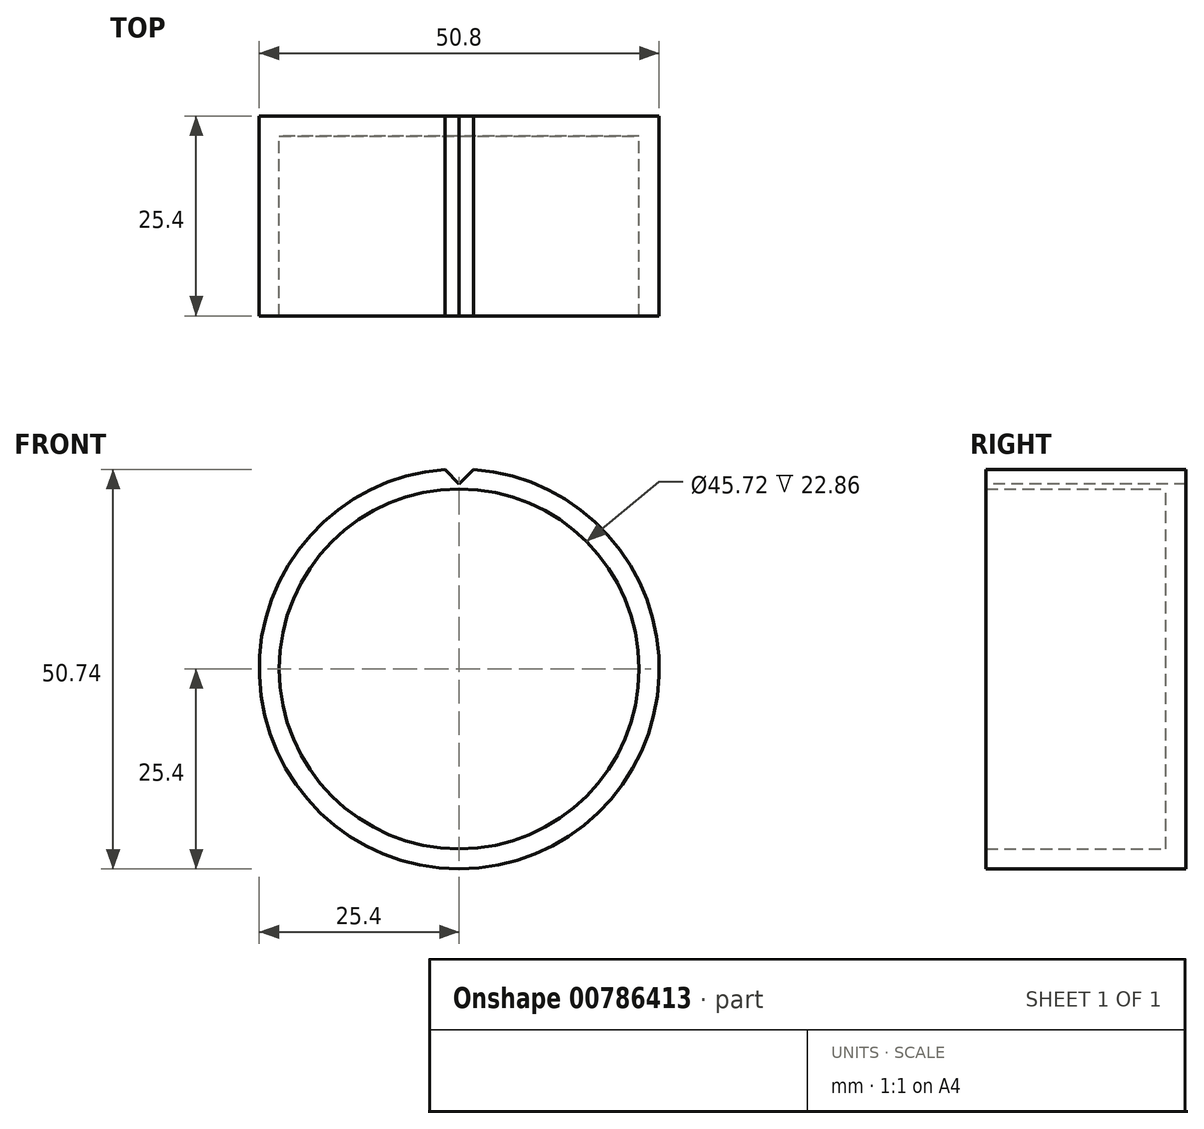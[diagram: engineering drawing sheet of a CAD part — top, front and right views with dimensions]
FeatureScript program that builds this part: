
annotation { "Feature Type Name" : "Feature", "Feature Type Description" : "" }
export const myFeature = defineFeature(function(context is Context, id is Id, definition is map)
    precondition{}
    {
        {
            var Q0;
            Q0=qCreatedBy(makeId("Front.planeOp"),FACE);
            var sketch = newSketch(context, id + "F0", { "sketchPlane" : qUnion([Q0])});
            skCircle(sketch, "E0", {"center": v(0, 0) * mm, "radius": 25.4 * mm});
            skSolve(sketch);
        }
        {
            var Q0;
            Q0 = qSketchRegion(id + "F0", true);
            extrude(context, id + "F1", {"entities" : qUnion([Q0]), "depth" : 25.4 * mm, "offsetDistance" : 25.4 * mm});
        }
        {
            var Q0;
            Q0=makeQuery(id+"F1.opExtrude","CAP_FACE",FACE,{"disambiguationData":[OSD([sQuery(id+"F0.wireOp",EDGE,"E0")])],"isStart":false});
            shell(context, id + "F2", {"entities" : qUnion([Q0]), "thickness" : 2.54 * mm});
        }
        {
            var Q0;
            Q0=makeQuery(id+"F1.opExtrude","CAP_FACE",FACE,{"disambiguationData":[OSD([sQuery(id+"F0.wireOp",EDGE,"E0")])],"isStart":false});
            cPlane(context, id + "F3", {"entities" : qUnion([Q0]), "cplaneType" : CPlaneType.OFFSET, "offset" : 0 * mm, "width" : 152.4 * mm, "height" : 152.4 * mm});
        }
        {
            var Q0;
            Q0=qCreatedBy(id+"F3.planeOp",FACE);
            var sketch = newSketch(context, id + "F4", { "sketchPlane" : qUnion([Q0])});
            skLineSegment(sketch, "E1", {"start": v(-1.93, 25.46) * mm, "end": v(0, 23.52) * mm});
            skLineSegment(sketch, "E2", {"start": v(0, 23.52) * mm, "end": v(1.94, 25.45) * mm});
            skLineSegment(sketch, "E3", {"start": v(-1.93, 25.46) * mm, "end": v(1.94, 25.45) * mm});
            skSolve(sketch);
        }
        {
            var Q0;
            Q0=qCreatedBy(makeId("Top.planeOp"),FACE);
            var sketch = newSketch(context, id + "F5", { "sketchPlane" : qUnion([Q0])});
            skLineSegment(sketch, "E4", {"start": v(0, 33.1) * mm, "end": v(0, -42.3) * mm});
            skSolve(sketch);
        }
        {
            var Q0;
            Q0=makeQuery(id+"F4.imprint","IMPRINT",FACE,{"disambiguationData":[TD([[makeQuery(id+"F4.imprint","IMPRINT",EDGE,{"derivedFrom":sQuery(id+"F4.wireOp",EDGE,"E1")}),1.0]])]});
            var Q1;
            Q1=makeQuery(id+"FBpxo5HtKtLYQ7g_2.39.F4.imprint","IMPRINT",FACE,{"disambiguationData":[TD([[makeQuery(id+"FBpxo5HtKtLYQ7g_2.39.F4.imprint","IMPRINT",EDGE,{"derivedFrom":sQuery(id+"FBpxo5HtKtLYQ7g_2.39.F4.wireOp",EDGE,"E1")}),1.0]])]});
            var Q2;
            Q2=makeQuery(id+"FBpxo5HtKtLYQ7g_2.38.F4.imprint","IMPRINT",FACE,{"disambiguationData":[TD([[makeQuery(id+"FBpxo5HtKtLYQ7g_2.38.F4.imprint","IMPRINT",EDGE,{"derivedFrom":sQuery(id+"FBpxo5HtKtLYQ7g_2.38.F4.wireOp",EDGE,"E1")}),1.0]])]});
            var Q3;
            Q3=makeQuery(id+"FBpxo5HtKtLYQ7g_2.37.F4.imprint","IMPRINT",FACE,{"disambiguationData":[TD([[makeQuery(id+"FBpxo5HtKtLYQ7g_2.37.F4.imprint","IMPRINT",EDGE,{"derivedFrom":sQuery(id+"FBpxo5HtKtLYQ7g_2.37.F4.wireOp",EDGE,"E1")}),1.0]])]});
            var Q4;
            Q4=makeQuery(id+"FBpxo5HtKtLYQ7g_2.36.F4.imprint","IMPRINT",FACE,{"disambiguationData":[TD([[makeQuery(id+"FBpxo5HtKtLYQ7g_2.36.F4.imprint","IMPRINT",EDGE,{"derivedFrom":sQuery(id+"FBpxo5HtKtLYQ7g_2.36.F4.wireOp",EDGE,"E1")}),1.0]])]});
            var Q5;
            Q5=makeQuery(id+"FBpxo5HtKtLYQ7g_2.35.F4.imprint","IMPRINT",FACE,{"disambiguationData":[TD([[makeQuery(id+"FBpxo5HtKtLYQ7g_2.35.F4.imprint","IMPRINT",EDGE,{"derivedFrom":sQuery(id+"FBpxo5HtKtLYQ7g_2.35.F4.wireOp",EDGE,"E1")}),1.0]])]});
            var Q6;
            Q6=makeQuery(id+"FBpxo5HtKtLYQ7g_2.34.F4.imprint","IMPRINT",FACE,{"disambiguationData":[TD([[makeQuery(id+"FBpxo5HtKtLYQ7g_2.34.F4.imprint","IMPRINT",EDGE,{"derivedFrom":sQuery(id+"FBpxo5HtKtLYQ7g_2.34.F4.wireOp",EDGE,"E1")}),1.0]])]});
            var Q7;
            Q7=makeQuery(id+"FBpxo5HtKtLYQ7g_2.33.F4.imprint","IMPRINT",FACE,{"disambiguationData":[TD([[makeQuery(id+"FBpxo5HtKtLYQ7g_2.33.F4.imprint","IMPRINT",EDGE,{"derivedFrom":sQuery(id+"FBpxo5HtKtLYQ7g_2.33.F4.wireOp",EDGE,"E1")}),1.0]])]});
            var Q8;
            Q8=makeQuery(id+"FBpxo5HtKtLYQ7g_2.32.F4.imprint","IMPRINT",FACE,{"disambiguationData":[TD([[makeQuery(id+"FBpxo5HtKtLYQ7g_2.32.F4.imprint","IMPRINT",EDGE,{"derivedFrom":sQuery(id+"FBpxo5HtKtLYQ7g_2.32.F4.wireOp",EDGE,"E1")}),1.0]])]});
            var Q9;
            Q9=makeQuery(id+"FBpxo5HtKtLYQ7g_2.31.F4.imprint","IMPRINT",FACE,{"disambiguationData":[TD([[makeQuery(id+"FBpxo5HtKtLYQ7g_2.31.F4.imprint","IMPRINT",EDGE,{"derivedFrom":sQuery(id+"FBpxo5HtKtLYQ7g_2.31.F4.wireOp",EDGE,"E1")}),1.0]])]});
            var Q10;
            Q10=makeQuery(id+"FBpxo5HtKtLYQ7g_2.30.F4.imprint","IMPRINT",FACE,{"disambiguationData":[TD([[makeQuery(id+"FBpxo5HtKtLYQ7g_2.30.F4.imprint","IMPRINT",EDGE,{"derivedFrom":sQuery(id+"FBpxo5HtKtLYQ7g_2.30.F4.wireOp",EDGE,"E1")}),1.0]])]});
            var Q11;
            Q11=makeQuery(id+"FBpxo5HtKtLYQ7g_2.29.F4.imprint","IMPRINT",FACE,{"disambiguationData":[TD([[makeQuery(id+"FBpxo5HtKtLYQ7g_2.29.F4.imprint","IMPRINT",EDGE,{"derivedFrom":sQuery(id+"FBpxo5HtKtLYQ7g_2.29.F4.wireOp",EDGE,"E1")}),1.0]])]});
            var Q12;
            Q12=makeQuery(id+"FBpxo5HtKtLYQ7g_2.28.F4.imprint","IMPRINT",FACE,{"disambiguationData":[TD([[makeQuery(id+"FBpxo5HtKtLYQ7g_2.28.F4.imprint","IMPRINT",EDGE,{"derivedFrom":sQuery(id+"FBpxo5HtKtLYQ7g_2.28.F4.wireOp",EDGE,"E1")}),1.0]])]});
            var Q13;
            Q13=makeQuery(id+"FBpxo5HtKtLYQ7g_2.27.F4.imprint","IMPRINT",FACE,{"disambiguationData":[TD([[makeQuery(id+"FBpxo5HtKtLYQ7g_2.27.F4.imprint","IMPRINT",EDGE,{"derivedFrom":sQuery(id+"FBpxo5HtKtLYQ7g_2.27.F4.wireOp",EDGE,"E1")}),1.0]])]});
            var Q14;
            Q14=makeQuery(id+"FBpxo5HtKtLYQ7g_2.26.F4.imprint","IMPRINT",FACE,{"disambiguationData":[TD([[makeQuery(id+"FBpxo5HtKtLYQ7g_2.26.F4.imprint","IMPRINT",EDGE,{"derivedFrom":sQuery(id+"FBpxo5HtKtLYQ7g_2.26.F4.wireOp",EDGE,"E1")}),1.0]])]});
            var Q15;
            Q15=makeQuery(id+"FBpxo5HtKtLYQ7g_2.25.F4.imprint","IMPRINT",FACE,{"disambiguationData":[TD([[makeQuery(id+"FBpxo5HtKtLYQ7g_2.25.F4.imprint","IMPRINT",EDGE,{"derivedFrom":sQuery(id+"FBpxo5HtKtLYQ7g_2.25.F4.wireOp",EDGE,"E1")}),1.0]])]});
            var Q16;
            Q16=makeQuery(id+"FBpxo5HtKtLYQ7g_2.24.F4.imprint","IMPRINT",FACE,{"disambiguationData":[TD([[makeQuery(id+"FBpxo5HtKtLYQ7g_2.24.F4.imprint","IMPRINT",EDGE,{"derivedFrom":sQuery(id+"FBpxo5HtKtLYQ7g_2.24.F4.wireOp",EDGE,"E1")}),1.0]])]});
            var Q17;
            Q17=makeQuery(id+"FBpxo5HtKtLYQ7g_2.23.F4.imprint","IMPRINT",FACE,{"disambiguationData":[TD([[makeQuery(id+"FBpxo5HtKtLYQ7g_2.23.F4.imprint","IMPRINT",EDGE,{"derivedFrom":sQuery(id+"FBpxo5HtKtLYQ7g_2.23.F4.wireOp",EDGE,"E1")}),1.0]])]});
            var Q18;
            Q18=makeQuery(id+"FBpxo5HtKtLYQ7g_2.22.F4.imprint","IMPRINT",FACE,{"disambiguationData":[TD([[makeQuery(id+"FBpxo5HtKtLYQ7g_2.22.F4.imprint","IMPRINT",EDGE,{"derivedFrom":sQuery(id+"FBpxo5HtKtLYQ7g_2.22.F4.wireOp",EDGE,"E1")}),1.0]])]});
            var Q19;
            Q19=makeQuery(id+"FBpxo5HtKtLYQ7g_2.21.F4.imprint","IMPRINT",FACE,{"disambiguationData":[TD([[makeQuery(id+"FBpxo5HtKtLYQ7g_2.21.F4.imprint","IMPRINT",EDGE,{"derivedFrom":sQuery(id+"FBpxo5HtKtLYQ7g_2.21.F4.wireOp",EDGE,"E1")}),1.0]])]});
            var Q20;
            Q20=makeQuery(id+"FBpxo5HtKtLYQ7g_2.20.F4.imprint","IMPRINT",FACE,{"disambiguationData":[TD([[makeQuery(id+"FBpxo5HtKtLYQ7g_2.20.F4.imprint","IMPRINT",EDGE,{"derivedFrom":sQuery(id+"FBpxo5HtKtLYQ7g_2.20.F4.wireOp",EDGE,"E1")}),1.0]])]});
            var Q21;
            Q21=makeQuery(id+"FBpxo5HtKtLYQ7g_2.19.F4.imprint","IMPRINT",FACE,{"disambiguationData":[TD([[makeQuery(id+"FBpxo5HtKtLYQ7g_2.19.F4.imprint","IMPRINT",EDGE,{"derivedFrom":sQuery(id+"FBpxo5HtKtLYQ7g_2.19.F4.wireOp",EDGE,"E1")}),1.0]])]});
            var Q22;
            Q22=makeQuery(id+"FBpxo5HtKtLYQ7g_2.18.F4.imprint","IMPRINT",FACE,{"disambiguationData":[TD([[makeQuery(id+"FBpxo5HtKtLYQ7g_2.18.F4.imprint","IMPRINT",EDGE,{"derivedFrom":sQuery(id+"FBpxo5HtKtLYQ7g_2.18.F4.wireOp",EDGE,"E1")}),1.0]])]});
            var Q23;
            Q23=makeQuery(id+"FBpxo5HtKtLYQ7g_2.17.F4.imprint","IMPRINT",FACE,{"disambiguationData":[TD([[makeQuery(id+"FBpxo5HtKtLYQ7g_2.17.F4.imprint","IMPRINT",EDGE,{"derivedFrom":sQuery(id+"FBpxo5HtKtLYQ7g_2.17.F4.wireOp",EDGE,"E1")}),1.0]])]});
            var Q24;
            Q24=makeQuery(id+"FBpxo5HtKtLYQ7g_2.16.F4.imprint","IMPRINT",FACE,{"disambiguationData":[TD([[makeQuery(id+"FBpxo5HtKtLYQ7g_2.16.F4.imprint","IMPRINT",EDGE,{"derivedFrom":sQuery(id+"FBpxo5HtKtLYQ7g_2.16.F4.wireOp",EDGE,"E1")}),1.0]])]});
            var Q25;
            Q25=makeQuery(id+"FBpxo5HtKtLYQ7g_2.15.F4.imprint","IMPRINT",FACE,{"disambiguationData":[TD([[makeQuery(id+"FBpxo5HtKtLYQ7g_2.15.F4.imprint","IMPRINT",EDGE,{"derivedFrom":sQuery(id+"FBpxo5HtKtLYQ7g_2.15.F4.wireOp",EDGE,"E1")}),1.0]])]});
            var Q26;
            Q26=makeQuery(id+"FBpxo5HtKtLYQ7g_2.14.F4.imprint","IMPRINT",FACE,{"disambiguationData":[TD([[makeQuery(id+"FBpxo5HtKtLYQ7g_2.14.F4.imprint","IMPRINT",EDGE,{"derivedFrom":sQuery(id+"FBpxo5HtKtLYQ7g_2.14.F4.wireOp",EDGE,"E1")}),1.0]])]});
            var Q27;
            Q27=makeQuery(id+"FBpxo5HtKtLYQ7g_2.13.F4.imprint","IMPRINT",FACE,{"disambiguationData":[TD([[makeQuery(id+"FBpxo5HtKtLYQ7g_2.13.F4.imprint","IMPRINT",EDGE,{"derivedFrom":sQuery(id+"FBpxo5HtKtLYQ7g_2.13.F4.wireOp",EDGE,"E1")}),1.0]])]});
            var Q28;
            Q28=makeQuery(id+"FBpxo5HtKtLYQ7g_2.12.F4.imprint","IMPRINT",FACE,{"disambiguationData":[TD([[makeQuery(id+"FBpxo5HtKtLYQ7g_2.12.F4.imprint","IMPRINT",EDGE,{"derivedFrom":sQuery(id+"FBpxo5HtKtLYQ7g_2.12.F4.wireOp",EDGE,"E1")}),1.0]])]});
            var Q29;
            Q29=makeQuery(id+"FBpxo5HtKtLYQ7g_2.11.F4.imprint","IMPRINT",FACE,{"disambiguationData":[TD([[makeQuery(id+"FBpxo5HtKtLYQ7g_2.11.F4.imprint","IMPRINT",EDGE,{"derivedFrom":sQuery(id+"FBpxo5HtKtLYQ7g_2.11.F4.wireOp",EDGE,"E1")}),1.0]])]});
            var Q30;
            Q30=makeQuery(id+"FBpxo5HtKtLYQ7g_2.10.F4.imprint","IMPRINT",FACE,{"disambiguationData":[TD([[makeQuery(id+"FBpxo5HtKtLYQ7g_2.10.F4.imprint","IMPRINT",EDGE,{"derivedFrom":sQuery(id+"FBpxo5HtKtLYQ7g_2.10.F4.wireOp",EDGE,"E1")}),1.0]])]});
            var Q31;
            Q31=makeQuery(id+"FBpxo5HtKtLYQ7g_2.9.F4.imprint","IMPRINT",FACE,{"disambiguationData":[TD([[makeQuery(id+"FBpxo5HtKtLYQ7g_2.9.F4.imprint","IMPRINT",EDGE,{"derivedFrom":sQuery(id+"FBpxo5HtKtLYQ7g_2.9.F4.wireOp",EDGE,"E1")}),1.0]])]});
            var Q32;
            Q32=makeQuery(id+"FBpxo5HtKtLYQ7g_2.8.F4.imprint","IMPRINT",FACE,{"disambiguationData":[TD([[makeQuery(id+"FBpxo5HtKtLYQ7g_2.8.F4.imprint","IMPRINT",EDGE,{"derivedFrom":sQuery(id+"FBpxo5HtKtLYQ7g_2.8.F4.wireOp",EDGE,"E1")}),1.0]])]});
            var Q33;
            Q33=makeQuery(id+"FBpxo5HtKtLYQ7g_2.7.F4.imprint","IMPRINT",FACE,{"disambiguationData":[TD([[makeQuery(id+"FBpxo5HtKtLYQ7g_2.7.F4.imprint","IMPRINT",EDGE,{"derivedFrom":sQuery(id+"FBpxo5HtKtLYQ7g_2.7.F4.wireOp",EDGE,"E1")}),1.0]])]});
            var Q34;
            Q34=makeQuery(id+"FBpxo5HtKtLYQ7g_2.6.F4.imprint","IMPRINT",FACE,{"disambiguationData":[TD([[makeQuery(id+"FBpxo5HtKtLYQ7g_2.6.F4.imprint","IMPRINT",EDGE,{"derivedFrom":sQuery(id+"FBpxo5HtKtLYQ7g_2.6.F4.wireOp",EDGE,"E1")}),1.0]])]});
            var Q35;
            Q35=makeQuery(id+"FBpxo5HtKtLYQ7g_2.5.F4.imprint","IMPRINT",FACE,{"disambiguationData":[TD([[makeQuery(id+"FBpxo5HtKtLYQ7g_2.5.F4.imprint","IMPRINT",EDGE,{"derivedFrom":sQuery(id+"FBpxo5HtKtLYQ7g_2.5.F4.wireOp",EDGE,"E1")}),1.0]])]});
            var Q36;
            Q36=makeQuery(id+"FBpxo5HtKtLYQ7g_2.4.F4.imprint","IMPRINT",FACE,{"disambiguationData":[TD([[makeQuery(id+"FBpxo5HtKtLYQ7g_2.4.F4.imprint","IMPRINT",EDGE,{"derivedFrom":sQuery(id+"FBpxo5HtKtLYQ7g_2.4.F4.wireOp",EDGE,"E1")}),1.0]])]});
            var Q37;
            Q37=makeQuery(id+"FBpxo5HtKtLYQ7g_2.3.F4.imprint","IMPRINT",FACE,{"disambiguationData":[TD([[makeQuery(id+"FBpxo5HtKtLYQ7g_2.3.F4.imprint","IMPRINT",EDGE,{"derivedFrom":sQuery(id+"FBpxo5HtKtLYQ7g_2.3.F4.wireOp",EDGE,"E1")}),1.0]])]});
            var Q38;
            Q38=makeQuery(id+"FBpxo5HtKtLYQ7g_2.2.F4.imprint","IMPRINT",FACE,{"disambiguationData":[TD([[makeQuery(id+"FBpxo5HtKtLYQ7g_2.2.F4.imprint","IMPRINT",EDGE,{"derivedFrom":sQuery(id+"FBpxo5HtKtLYQ7g_2.2.F4.wireOp",EDGE,"E1")}),1.0]])]});
            var Q39;
            Q39=makeQuery(id+"FBpxo5HtKtLYQ7g_2.1.F4.imprint","IMPRINT",FACE,{"disambiguationData":[TD([[makeQuery(id+"FBpxo5HtKtLYQ7g_2.1.F4.imprint","IMPRINT",EDGE,{"derivedFrom":sQuery(id+"FBpxo5HtKtLYQ7g_2.1.F4.wireOp",EDGE,"E1")}),1.0]])]});
            extrude(context, id + "F6", {"entities" : qUnion([Q0, Q1, Q2, Q3, Q4, Q5, Q6, Q7, Q8, Q9, Q10, Q11, Q12, Q13, Q14, Q15, Q16, Q17, Q18, Q19, Q20, Q21, Q22, Q23, Q24, Q25, Q26, Q27, Q28, Q29, Q30, Q31, Q32, Q33, Q34, Q35, Q36, Q37, Q38, Q39]), "operationType" : NewBodyOperationType.REMOVE, "oppositeDirection" : true, "depth" : 25.4 * mm, "offsetDistance" : 25.4 * mm});
        }
    });
